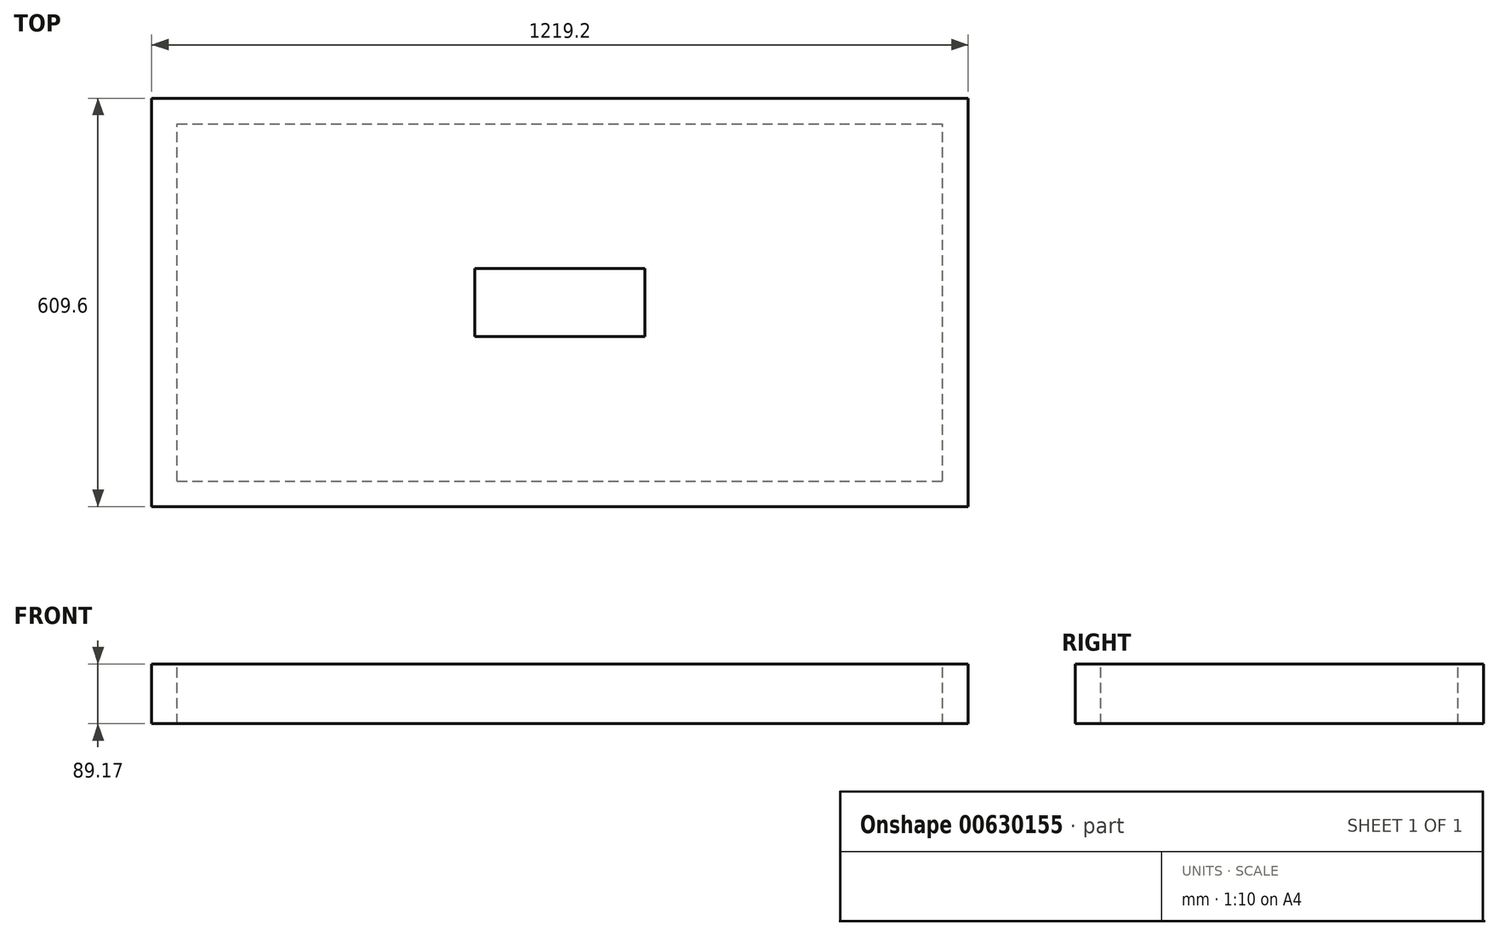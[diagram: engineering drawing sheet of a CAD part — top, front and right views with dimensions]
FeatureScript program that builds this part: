
annotation { "Feature Type Name" : "Feature", "Feature Type Description" : "" }
export const myFeature = defineFeature(function(context is Context, id is Id, definition is map)
    precondition{}
    {
        {
            var Q0;
            Q0=qCreatedBy(makeId("Top.planeOp"),FACE);
            var sketch = newSketch(context, id + "F0", { "sketchPlane" : qUnion([Q0])});
            skLineSegment(sketch, "E0.bottom", {"start": v(-1219.2, 127.35) * mm, "end": v(0, 127.35) * mm});
            skLineSegment(sketch, "E0.top", {"start": v(-1219.2, -482.25) * mm, "end": v(0, -482.25) * mm});
            skLineSegment(sketch, "E0.left", {"start": v(-1219.2, 127.35) * mm, "end": v(-1219.2, -482.25) * mm});
            skLineSegment(sketch, "E0.right", {"start": v(0, 127.35) * mm, "end": v(0, -482.25) * mm});
            skSolve(sketch);
        }
        {
            var Q0;
            Q0=makeQuery(id+"F0.imprint","IMPRINT",FACE,{"disambiguationData":[TD([[makeQuery(id+"F0.imprint","IMPRINT",EDGE,{"derivedFrom":sQuery(id+"F0.wireOp",EDGE,"E0.bottom")}),-1.0]])]});
            extrude(context, id + "F1", {"entities" : qUnion([Q0]), "depth" : 1 / 50.8 * mm, "offsetDistance" : 25.4 * mm});
        }
        {
            var Q0;
            Q0=makeQuery(id+"F1.opExtrude","CAP_FACE",FACE,{"disambiguationData":[OSD([sQuery(id+"F0.wireOp",EDGE,"E0.bottom"),sQuery(id+"F0.wireOp",EDGE,"E0.top"),sQuery(id+"F0.wireOp",EDGE,"E0.left"),sQuery(id+"F0.wireOp",EDGE,"E0.right")])],"isStart":true});
            var sketch = newSketch(context, id + "F2", { "sketchPlane" : qUnion([Q0])});
            skLineSegment(sketch, "E1.bottom", {"start": v(-1219.2, 482.25) * mm, "end": v(0, 482.25) * mm});
            skLineSegment(sketch, "E1.top", {"start": v(-1219.2, 444.15) * mm, "end": v(0, 444.15) * mm});
            skLineSegment(sketch, "E1.left", {"start": v(-1219.2, 482.25) * mm, "end": v(-1219.2, 444.15) * mm});
            skLineSegment(sketch, "E1.right", {"start": v(0, 482.25) * mm, "end": v(0, 444.15) * mm});
            skLineSegment(sketch, "E2.bottom", {"start": v(-1219.2, -127.35) * mm, "end": v(0, -127.35) * mm});
            skLineSegment(sketch, "E2.top", {"start": v(-1219.2, -89.25) * mm, "end": v(0, -89.25) * mm});
            skLineSegment(sketch, "E2.left", {"start": v(-1219.2, -127.35) * mm, "end": v(-1219.2, -89.25) * mm});
            skLineSegment(sketch, "E2.right", {"start": v(0, -127.35) * mm, "end": v(0, -89.25) * mm});
            skLineSegment(sketch, "E3.bottom", {"start": v(-1219.2, 444.15) * mm, "end": v(-1167.37, 444.15) * mm});
            skLineSegment(sketch, "E3.top", {"start": v(-1219.2, -89.25) * mm, "end": v(-1167.37, -89.25) * mm});
            skLineSegment(sketch, "E3.left", {"start": v(-1219.2, 444.15) * mm, "end": v(-1219.2, -89.25) * mm});
            skLineSegment(sketch, "E4.bottom", {"start": v(0, 444.15) * mm, "end": v(-38.1, 444.15) * mm});
            skLineSegment(sketch, "E4.top", {"start": v(0, -89.25) * mm, "end": v(-38.1, -89.25) * mm});
            skLineSegment(sketch, "E4.left", {"start": v(0, 444.15) * mm, "end": v(0, -89.25) * mm});
            skLineSegment(sketch, "E4.right", {"start": v(-38.1, 444.15) * mm, "end": v(-38.1, -89.25) * mm});
            skLineSegment(sketch, "E5", {"start": v(-1181.1, 444.15) * mm, "end": v(-1181.1, -89.25) * mm});
            skSolve(sketch);
        }
        {
            var Q0;
            Q0=makeQuery(id+"F2.imprint","IMPRINT",FACE,{"disambiguationData":[TD([[makeQuery(id+"F2.imprint","IMPRINT",EDGE,{"derivedFrom":sQuery(id+"F2.wireOp",EDGE,"E2.bottom")}),1.0]])]});
            var Q1;
            Q1=makeQuery(id+"F2.imprint","IMPRINT",FACE,{"disambiguationData":[TD([[makeQuery(id+"F2.imprint","IMPRINT",EDGE,{"derivedFrom":sQuery(id+"F2.wireOp",EDGE,"E1.bottom")}),-1.0]])]});
            var Q2;
            {var subQ0=sQuery(id+"F2.wireOp",EDGE,"E3.left");Q2=makeQuery(id+"F2.imprint","IMPRINT",FACE,{"disambiguationData":[TD([[makeQuery(id+"F2.imprint","IMPRINT",EDGE,{"derivedFrom":subQ0}),-1.0]])]});}
            var Q3;
            {var subQ0=sQuery(id+"F2.wireOp",EDGE,"E4.left");Q3=makeQuery(id+"F2.imprint","IMPRINT",FACE,{"disambiguationData":[TD([[makeQuery(id+"F2.imprint","IMPRINT",EDGE,{"derivedFrom":subQ0}),1.0]])]});}
            extrude(context, id + "F3", {"entities" : qUnion([Q0, Q1, Q2, Q3]), "operationType" : NewBodyOperationType.ADD, "depth" : 88.9 * mm, "offsetDistance" : 25.4 * mm});
        }
        {
            var Q0;
            Q0=makeQuery(id+"F1.opExtrude","CAP_FACE",FACE,{"disambiguationData":[OSD([sQuery(id+"F0.wireOp",EDGE,"E0.bottom"),sQuery(id+"F0.wireOp",EDGE,"E0.top"),sQuery(id+"F0.wireOp",EDGE,"E0.left"),sQuery(id+"F0.wireOp",EDGE,"E0.right")])],"isStart":false});
            var sketch = newSketch(context, id + "F4", { "sketchPlane" : qUnion([Q0])});
            skLineSegment(sketch, "E6.bottom", {"start": v(-736.6, -126.65) * mm, "end": v(-482.6, -126.65) * mm});
            skLineSegment(sketch, "E6.top", {"start": v(-736.6, -228.25) * mm, "end": v(-482.6, -228.25) * mm});
            skLineSegment(sketch, "E6.left", {"start": v(-736.6, -126.65) * mm, "end": v(-736.6, -228.25) * mm});
            skLineSegment(sketch, "E6.right", {"start": v(-482.6, -126.65) * mm, "end": v(-482.6, -228.25) * mm});
            skSolve(sketch);
        }
        {
            var Q0;
            Q0=makeQuery(id+"F4.imprint","IMPRINT",FACE,{"disambiguationData":[TD([[makeQuery(id+"F4.imprint","IMPRINT",EDGE,{"derivedFrom":sQuery(id+"F4.wireOp",EDGE,"E6.bottom")}),-1.0]])]});
            extrude(context, id + "F5", {"entities" : qUnion([Q0]), "operationType" : NewBodyOperationType.ADD, "depth" : 0.25 * mm, "offsetDistance" : 25.4 * mm});
        }
    });
